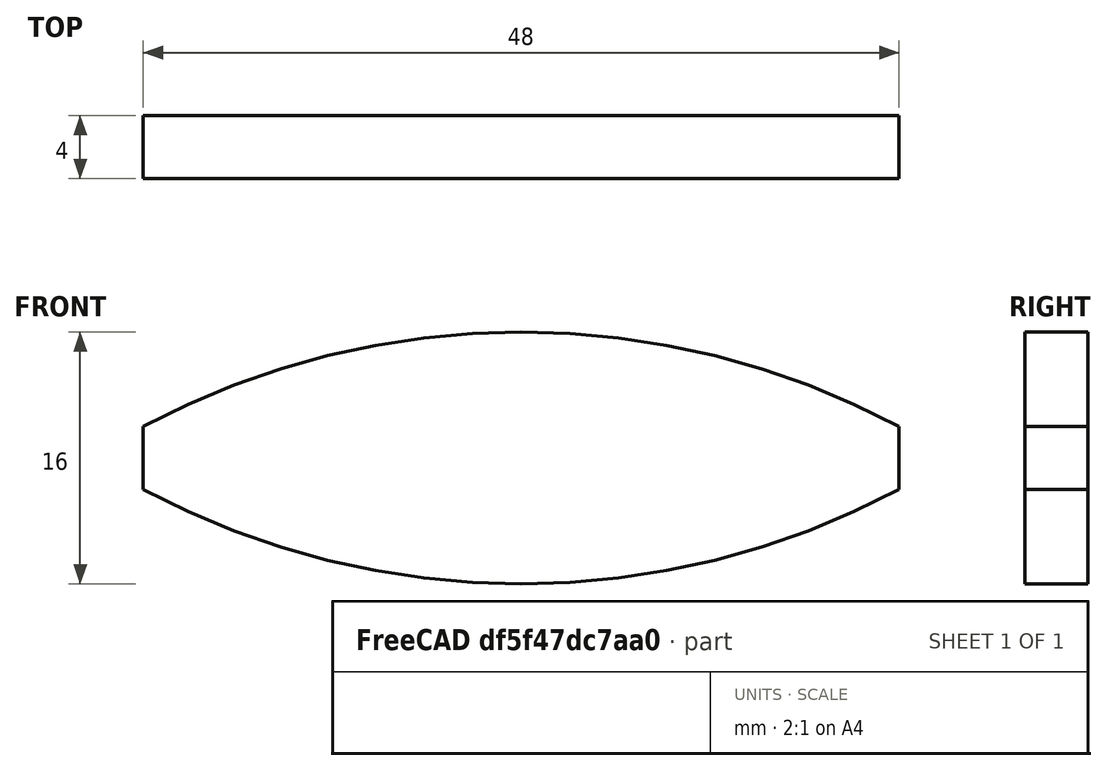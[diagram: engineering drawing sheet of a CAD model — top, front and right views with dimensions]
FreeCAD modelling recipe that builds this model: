
FCSTD DOCUMENT  (FreeCAD 1.1R20260325 (Git shallow))
Label: Biscuits_4_x_16_x_48_mm
License: All rights reserved
LicenseURL: http://en.wikipedia.org/wiki/All_rights_reserved
objects: App::LinkGroup×2, App::Point×2, Sketcher::SketchObject×1, Spreadsheet::Sheet×1, PartDesign::Pad×1, PartDesign::Body×1, App::Part×1
note: 6 computed .brp shape members not serialized (recipe doc carries the construction recipe); baked Part::Feature solids carry a one-line shape summary decoded from their .brp

FEATURE [Sketcher::SketchObject] Sketch
  ArcFitTolerance = 0
  AttachmentSupport = -> [XZ_Plane001]
  ExternalTypes = [0]
  FullyConstrained = false
  MakeInternals = false
  MapMode = 5
  Placement = pos=(0,0,0) rot=(1,0,0;1.5708rad)
  _ExternalGeoVersion = 0
  expr: Constraints[13] = <<settings>>.bw
  expr: Constraints[14] = <<settings>>.bh
  expr: Constraints[16] = <<settings>>.bw / 2
  sketch-geometry (6):
    g0: LineSegment StartX=-24 StartY=10 StartZ=0 EndX=-24 EndY=6 EndZ=0
    g1: LineSegment StartX=24 StartY=10 StartZ=0 EndX=24 EndY=6 EndZ=0
    g2: ArcOfCircle CenterX=0 CenterY=-35 CenterZ=0 NormalX=0 NormalY=0 NormalZ=1 AngleXU=0 Radius=51 StartAngle=1.08084 EndAngle=2.06075
    g3: ArcOfCircle CenterX=0 CenterY=51 CenterZ=0 NormalX=0 NormalY=0 NormalZ=1 AngleXU=0 Radius=51 StartAngle=4.22243 EndAngle=5.20235
    g4: LineSegment [constr] StartX=0 StartY=16 StartZ=0 EndX=0 EndY=0 EndZ=0
    g5: LineSegment [constr] StartX=-49.5813 StartY=8 StartZ=0 EndX=66.2857 EndY=8 EndZ=0
  constraints (18):
    c: Vertical(g0)
    c: Vertical(g1)
    c: Coincident(g2,g0)
    c: Coincident(g2,g1)
    c: Coincident(g3,g0)
    c: Coincident(g3,g1)
    c: PointOnObject(g4,g2)
    c: PointOnObject(g4,g3)
    c: Vertical(g4)
    c: Coincident(g4,g-1)
    c: Horizontal(g1,g0)
    c: DistanceY(g1,g1) = 4
    c: Vertical(g3,g4)
    c: DistanceY(g4,g4) = 16
    c: DistanceX(g0,g1) = 48
    c: Horizontal(g5)
    c: DistanceY(g4,g5) = 8
    c: Symmetric(g2,g3,g5)
FEATURE [Spreadsheet::Sheet] Spreadsheet  label="settings"
  cells = A1='Settings:; A2='Width; B2(bw)=16; A3='Height; B3(bh)=48
FEATURE [PartDesign::Pad] Pad
  Direction = (0,-1,2e-16)
  Length = 4
  Length2 = 10
  Placement = pos=(0,0,0) rot=(1,0,0;1.5708rad)
  Profile = -> Sketch
  ReferenceAxis = -> Sketch [N_Axis]
  SideType = 0
  Suppressed = false
  Type = 0
  Type2 = 0
FEATURE [PartDesign::Body] Body
  AllowCompound = true
  Group = -> [Sketch,Pad]
  Origin = -> Origin001
  Placement = pos=(0,2,0) rot=(0,0,1;0rad)
  Tip = -> Pad
FEATURE [App::Part] Part
  Group = -> [Body]
  Origin = -> Origin
FEATURE [App::LinkGroup] LinkGroup  label="Biscuits 4 x 16 x 48 mm, link this"
  ElementList = -> [Part]
  LinkMode = 0
FEATURE [App::LinkGroup] LinkGroup001  label="Biscuits 4 x 16 x 48 mm, hide this"
  ElementList = -> [LinkGroup]
  LinkMode = 0
FEATURE [App::Point] Origin002  label="Origin"
  Role = Origin
FEATURE [App::Point] Origin003  label="Origin"
  Role = Origin
